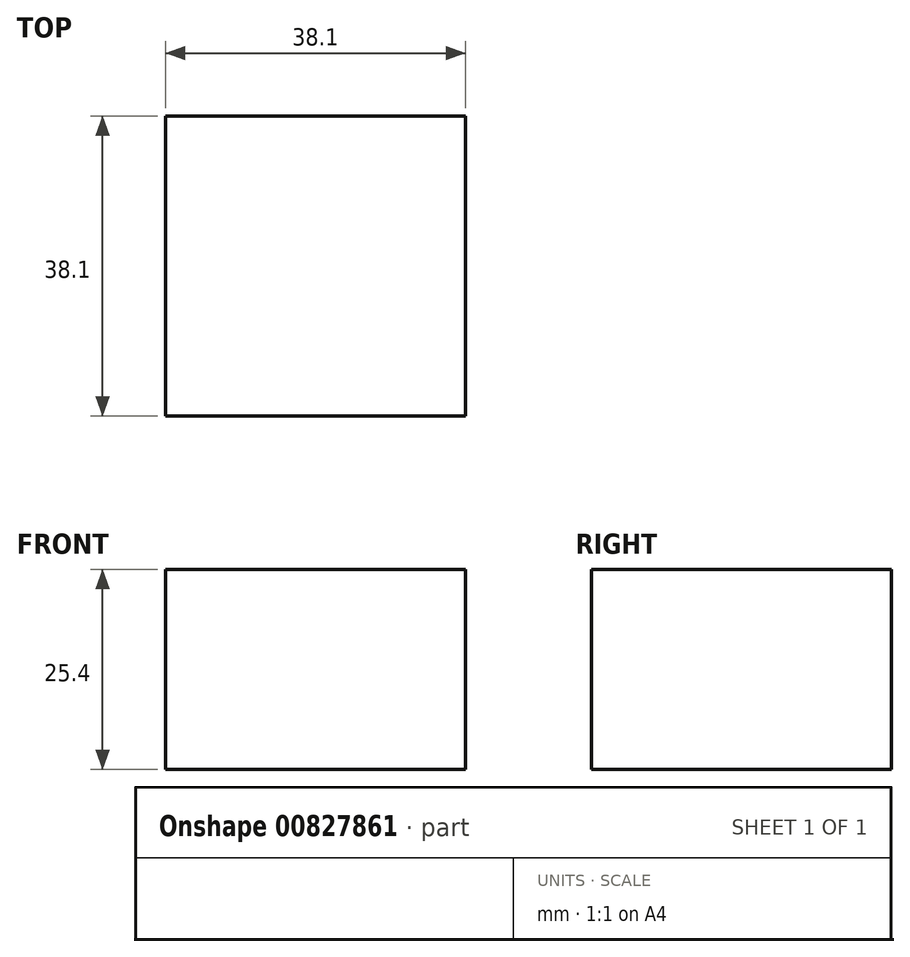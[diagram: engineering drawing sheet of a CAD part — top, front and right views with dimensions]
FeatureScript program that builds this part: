
annotation { "Feature Type Name" : "Feature", "Feature Type Description" : "" }
export const myFeature = defineFeature(function(context is Context, id is Id, definition is map)
    precondition{}
    {
        {
            var Q0;
            Q0=qCreatedBy(makeId("Top.planeOp"),FACE);
            var sketch = newSketch(context, id + "F0", { "sketchPlane" : qUnion([Q0])});
            skLineSegment(sketch, "E0", {"start": v(-19.05, 19.05) * mm, "end": v(19.05, 19.05) * mm});
            skLineSegment(sketch, "E1", {"start": v(19.05, 19.05) * mm, "end": v(19.05, -19.05) * mm});
            skLineSegment(sketch, "E2", {"start": v(19.05, -19.05) * mm, "end": v(-19.05, -19.05) * mm});
            skLineSegment(sketch, "E3", {"start": v(-19.05, -19.05) * mm, "end": v(-19.05, 19.05) * mm});
            skPoint(sketch, "E4", {"position": v(0, 19.05) * mm});
            skPoint(sketch, "E5", {"position": v(-19.05, 0) * mm});
            skSolve(sketch);
        }
        {
            var Q0;
            Q0=makeQuery(id+"F0.imprint","IMPRINT",FACE,{"disambiguationData":[TD([[makeQuery(id+"F0.imprint","IMPRINT",EDGE,{"derivedFrom":sQuery(id+"F0.wireOp",EDGE,"E0")}),-1.0]])]});
            extrude(context, id + "F1", {"entities" : qUnion([Q0]), "depth" : 25.4 * mm, "offsetDistance" : 25 * mm});
        }
    });
